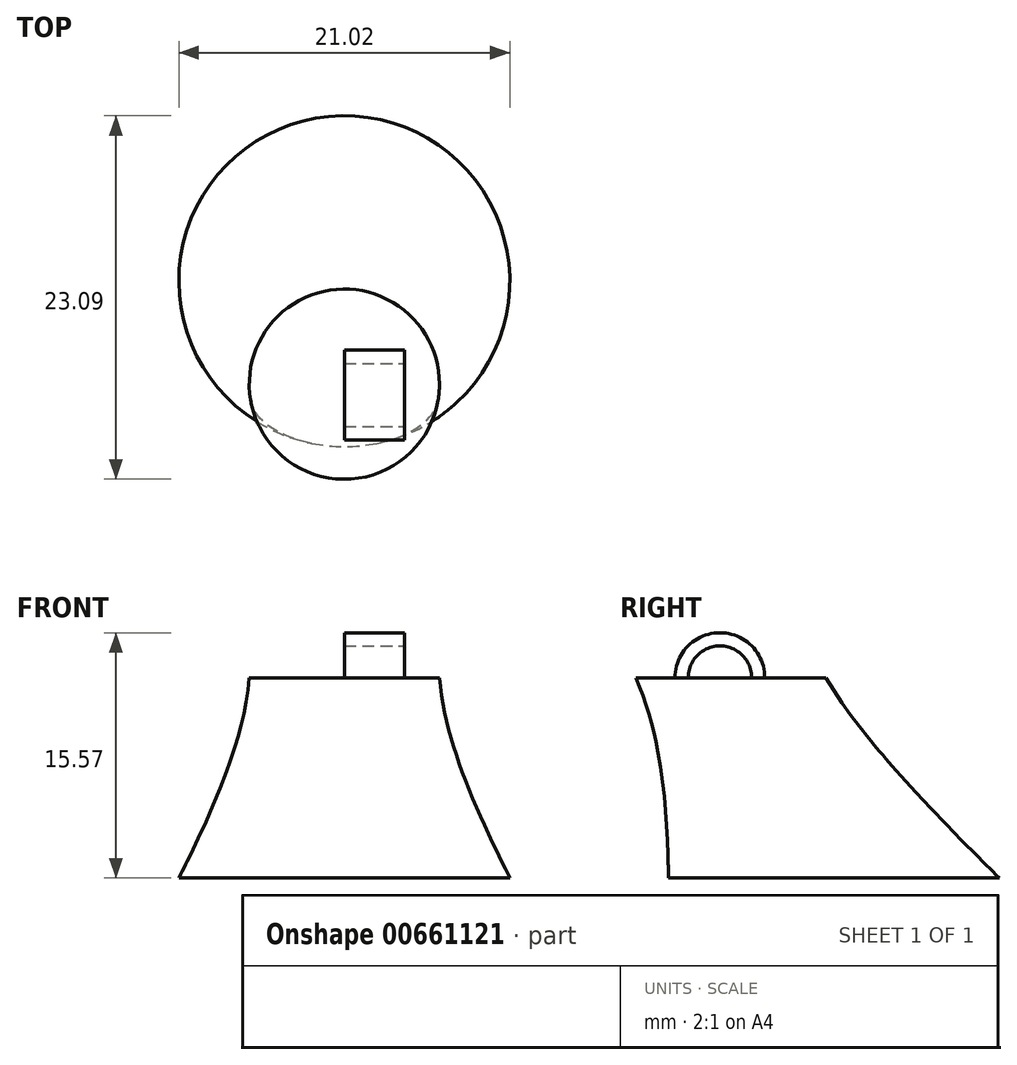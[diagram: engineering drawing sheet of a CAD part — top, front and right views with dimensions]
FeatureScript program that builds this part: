
annotation { "Feature Type Name" : "Feature", "Feature Type Description" : "" }
export const myFeature = defineFeature(function(context is Context, id is Id, definition is map)
    precondition{}
    {
        {
            var Q0;
            Q0=qCreatedBy(makeId("Top.planeOp"),FACE);
            var sketch = newSketch(context, id + "F0", { "sketchPlane" : qUnion([Q0])});
            skCircle(sketch, "E0", {"center": v(0, 0) * mm, "radius": 10.5 * mm});
            skSolve(sketch);
        }
        {
            var Q0;
            Q0=qCreatedBy(makeId("Top.planeOp"),FACE);
            cPlane(context, id + "F1", {"entities" : qUnion([Q0]), "cplaneType" : CPlaneType.OFFSET, "offset" : 12.7 * mm, "width" : 152.4 * mm, "height" : 152.4 * mm});
        }
        {
            var Q0;
            Q0=qCreatedBy(id+"F1.planeOp",FACE);
            var sketch = newSketch(context, id + "F2", { "sketchPlane" : qUnion([Q0])});
            skCircle(sketch, "E1", {"center": v(0, -6.54) * mm, "radius": 6.04 * mm});
            skSolve(sketch);
        }
        {
            var Q0;
            Q0=makeQuery(id+"F2.imprint","IMPRINT",FACE,{"disambiguationData":[TD([[makeQuery(id+"F2.imprint","IMPRINT",EDGE,{"derivedFrom":sQuery(id+"F2.wireOp",EDGE,"E1")}),1.0]])]});
            var Q1;
            Q1=makeQuery(id+"F0.imprint","IMPRINT",FACE,{"disambiguationData":[TD([[makeQuery(id+"F0.imprint","IMPRINT",EDGE,{"derivedFrom":sQuery(id+"F0.wireOp",EDGE,"E0")}),1.0]])]});
            loft(context, id + "F3", {"sheetProfilesArray" : [{ "sheetProfileEntities" : qUnion([Q0]) }, { "sheetProfileEntities" : qUnion([Q1]) }]});
        }
        {
            var Q0;
            Q0=qCreatedBy(makeId("Right.planeOp"),FACE);
            var sketch = newSketch(context, id + "F4", { "sketchPlane" : qUnion([Q0])});
            skCircle(sketch, "E2", {"center": v(-7.24, 12.72) * mm, "radius": 2.85 * mm});
            skSolve(sketch);
        }
        {
            var Q0;
            Q0=makeQuery(id+"F4.imprint","IMPRINT",FACE,{"disambiguationData":[TD([[makeQuery(id+"F4.imprint","IMPRINT",EDGE,{"derivedFrom":sQuery(id+"F4.wireOp",EDGE,"E2")}),1.0]])]});
            extrude(context, id + "F5", {"entities" : qUnion([Q0]), "operationType" : NewBodyOperationType.ADD, "depth" : 3.8 * mm, "offsetDistance" : 25.4 * mm});
        }
        {
            var Q0;
            Q0=makeQuery(id+"F5.opExtrude","CAP_FACE",FACE,{"disambiguationData":[OSD([sQuery(id+"F4.wireOp",EDGE,"E2")])],"isStart":false});
            var sketch = newSketch(context, id + "F6", { "sketchPlane" : qUnion([Q0])});
            skCircle(sketch, "E3", {"center": v(-7.24, 12.72) * mm, "radius": 2 * mm});
            skSolve(sketch);
        }
        {
            var Q0;
            {var subQ0=sQuery(id+"F6.wireOp",EDGE,"E3");var subQ1=makeQuery(id+"F5.boolean.opBoolean","INTERSECT",EDGE,{"derivedFrom":[makeQuery(id+"F3.opLoft","CAP_FACE",FACE,{"disambiguationData":[OSD([makeQuery(id+"F2.imprint","IMPRINT",FACE,{"disambiguationData":[TD([[makeQuery(id+"F2.imprint","IMPRINT",EDGE,{"derivedFrom":sQuery(id+"F2.wireOp",EDGE,"E1")}),1.0]])]})])],"isStart":true}),makeQuery(id+"F5.opExtrude","CAP_FACE",FACE,{"disambiguationData":[OSD([sQuery(id+"F4.wireOp",EDGE,"E2")])],"isStart":false})]});var subQ2=makeQuery(id+"F6.imprint","INTERSECT",VERTEX,{"disambiguationData":[OD(0.0)],"derivedFrom":[subQ1,subQ0]});Q0=makeQuery(id+"F6.imprint","IMPRINT",FACE,{"disambiguationData":[TD([[makeQuery(id+"F6.imprint","IMPRINT",EDGE,{"disambiguationData":[TD([[subQ2,1.0]])],"derivedFrom":subQ0}),1.0]])]});}
            extrude(context, id + "F7", {"entities" : qUnion([Q0]), "operationType" : NewBodyOperationType.REMOVE, "endBound" : BoundingType.THROUGH_ALL, "oppositeDirection" : true, "depth" : 25.4 * mm, "offsetDistance" : 25.4 * mm});
        }
    });
